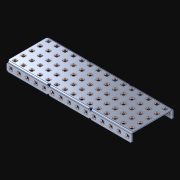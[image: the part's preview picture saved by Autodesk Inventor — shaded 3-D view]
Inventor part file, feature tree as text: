
AUTODESK INVENTOR PART (.ipt)
format: ipt  version: 2021 (Build 250183000, 183)  size: 1,814,016 bytes
history: native  units: in
note: dims shown in document units (in); Inventor stores cm internally (conversion verified against a paired STEP export)
features: extrude x106, other x106, sketch x4, pattern_linear x3
ambient origin geometry x8: Origin, YZ Plane, XZ Plane, XY Plane, X Axis, Y Axis, Z Axis, Center Point
bodies: Solid1 (feature_tree)
feature tree (219):
  pattern_linear  "Rectangular Pattern1"  Spacing1=0.182in  [1 undecoded]
  pattern_linear  "Rectangular Pattern2"  Spacing1=0.046in  [1 undecoded]
  pattern_linear  "Rectangular Pattern3"  Spacing1=0.5in  [1 undecoded]
  extrude  "Extrusion1"  Depth=0.046in
  sketch  "Sketch1"  dims[d0=0.182in]
  other  "Srf1"
  sketch  "Sketch2"  dims[d1=0.046in d2=0.0in]
  other  "Srf2"
  sketch  "Sketch3"  dims[d3=0.182in]
  other  "Srf3"
  other  "Srf4"
  other  "Srf5"
  other  "Srf6"
  other  "Srf7"
  other  "Srf8"
  other  "Srf9"
  other  "Srf10"
  other  "Srf11"
  other  "Srf12"
  other  "Srf13"
  other  "Srf14"
  other  "Srf15"
  other  "Srf16"
  other  "Srf17"
  other  "Srf38"
  other  "Srf39"
  other  "Srf40"
  other  "Srf41"
  other  "Srf42"
  other  "Srf43"
  other  "Srf44"
  other  "Srf45"
  other  "Srf46"
  other  "Srf47"
  other  "Srf48"
  other  "Srf49"
  other  "Srf50"
  other  "Srf51"
  other  "Srf72"
  other  "Srf73"
  other  "Srf74"
  other  "Srf75"
  other  "Srf76"
  other  "Srf77"
  other  "Srf78"
  other  "Srf79"
  other  "Srf80"
  other  "Srf81"
  other  "Srf82"
  other  "Srf83"
  other  "Srf84"
  other  "Srf85"
  other  "Srf86"
  other  "Srf107"
  other  "Srf108"
  other  "Srf109"
  other  "Srf110"
  other  "Srf111"
  other  "Srf112"
  other  "Srf113"
  other  "Srf114"
  other  "Srf115"
  other  "Srf116"
  other  "Srf117"
  other  "Srf118"
  other  "Srf119"
  other  "Srf120"
  other  "Srf121"
  other  "Srf142"
  other  "Srf143"
  other  "Srf144"
  other  "Srf145"
  other  "Srf146"
  other  "Srf147"
  other  "Srf148"
  other  "Srf149"
  other  "Srf150"
  other  "Srf151"
  other  "Srf152"
  other  "Srf153"
  other  "Srf154"
  other  "Srf155"
  other  "Srf156"
  other  "Srf177"
  other  "Srf178"
  other  "Srf179"
  other  "Srf180"
  other  "Srf181"
  other  "Srf182"
  other  "Srf183"
  other  "Srf184"
  other  "Srf185"
  other  "Srf186"
  other  "Srf187"
  other  "Srf188"
  other  "Srf189"
  other  "Srf190"
  other  "Srf191"
  other  "Srf212"
  other  "Srf213"
  other  "Srf214"
  other  "Srf215"
  other  "Srf216"
  other  "Srf217"
  other  "Srf218"
  other  "Srf219"
  other  "Srf220"
  other  "Srf221"
  other  "Srf222"
  other  "Srf223"
  other  "Srf224"
  other  "Srf225"
  sketch  "Sketch4"  dims[d4=0.046in d5=0.0in d6=0.182in d7=0.046in d8=0.0in d11=0.5in d12=5.9055in d14=0.5in d15=1.9685in d17=0.5in d18=5.9055in d20=0.5in d21=10.0in d22=0.0in]
  parser-record x1  (decoder bookkeeping rows leaked as tree rows — omitted from the tree; the rows remain in map.json)
  extrude  "ExtrusionSrf1"  Depth=0.046in
  extrude  "ExtrusionSrf2"  Depth=0.046in
  extrude  "ExtrusionSrf3"  Depth=0.046in
  extrude  "ExtrusionSrf4"  Depth=0.046in
  extrude  "ExtrusionSrf5"  Depth=0.046in
  extrude  "ExtrusionSrf6"  TaperAngle=0.0deg  [1 undecoded]
  extrude  "ExtrusionSrf7"  [1 undecoded]
  extrude  "ExtrusionSrf8"  [1 undecoded]
  extrude  "ExtrusionSrf9"  [1 undecoded]
  extrude  "ExtrusionSrf10"  [1 undecoded]
  extrude  "ExtrusionSrf11"  [1 undecoded]
  extrude  "ExtrusionSrf12"  [1 undecoded]
  extrude  "ExtrusionSrf13"  [1 undecoded]
  extrude  "ExtrusionSrf14"  [1 undecoded]
  extrude  "ExtrusionSrf15"  [1 undecoded]
  extrude  "ExtrusionSrf16"  [1 undecoded]
  extrude  "ExtrusionSrf17"  [1 undecoded]
  extrude  "ExtrusionSrf38"  [1 undecoded]
  extrude  "ExtrusionSrf39"  [1 undecoded]
  extrude  "ExtrusionSrf40"  [1 undecoded]
  extrude  "ExtrusionSrf41"  [1 undecoded]
  extrude  "ExtrusionSrf42"  [1 undecoded]
  extrude  "ExtrusionSrf43"  [1 undecoded]
  extrude  "ExtrusionSrf44"  [1 undecoded]
  extrude  "ExtrusionSrf45"  [1 undecoded]
  extrude  "ExtrusionSrf46"  [1 undecoded]
  extrude  "ExtrusionSrf47"  [1 undecoded]
  extrude  "ExtrusionSrf48"  [1 undecoded]
  extrude  "ExtrusionSrf49"  [1 undecoded]
  extrude  "ExtrusionSrf50"  [1 undecoded]
  extrude  "ExtrusionSrf51"  [1 undecoded]
  extrude  "ExtrusionSrf72"  [1 undecoded]
  extrude  "ExtrusionSrf73"  [1 undecoded]
  extrude  "ExtrusionSrf74"  [1 undecoded]
  extrude  "ExtrusionSrf75"  [1 undecoded]
  extrude  "ExtrusionSrf76"  [1 undecoded]
  extrude  "ExtrusionSrf77"  [1 undecoded]
  extrude  "ExtrusionSrf78"  [1 undecoded]
  extrude  "ExtrusionSrf79"  [1 undecoded]
  extrude  "ExtrusionSrf80"  [1 undecoded]
  extrude  "ExtrusionSrf81"  [1 undecoded]
  extrude  "ExtrusionSrf82"  [1 undecoded]
  extrude  "ExtrusionSrf83"  [1 undecoded]
  extrude  "ExtrusionSrf84"  [1 undecoded]
  extrude  "ExtrusionSrf85"  [1 undecoded]
  extrude  "ExtrusionSrf86"  [1 undecoded]
  extrude  "ExtrusionSrf107"  [1 undecoded]
  extrude  "ExtrusionSrf108"  [1 undecoded]
  extrude  "ExtrusionSrf109"  [1 undecoded]
  extrude  "ExtrusionSrf110"  [1 undecoded]
  extrude  "ExtrusionSrf111"  [1 undecoded]
  extrude  "ExtrusionSrf112"  [1 undecoded]
  extrude  "ExtrusionSrf113"  [1 undecoded]
  extrude  "ExtrusionSrf114"  [1 undecoded]
  extrude  "ExtrusionSrf115"  [1 undecoded]
  extrude  "ExtrusionSrf116"  [1 undecoded]
  extrude  "ExtrusionSrf117"  [1 undecoded]
  extrude  "ExtrusionSrf118"  [1 undecoded]
  extrude  "ExtrusionSrf119"  [1 undecoded]
  extrude  "ExtrusionSrf120"  [1 undecoded]
  extrude  "ExtrusionSrf121"  [1 undecoded]
  extrude  "ExtrusionSrf142"  [1 undecoded]
  extrude  "ExtrusionSrf143"  [1 undecoded]
  extrude  "ExtrusionSrf144"  [1 undecoded]
  extrude  "ExtrusionSrf145"  [1 undecoded]
  extrude  "ExtrusionSrf146"  [1 undecoded]
  extrude  "ExtrusionSrf147"  [1 undecoded]
  extrude  "ExtrusionSrf148"  [1 undecoded]
  extrude  "ExtrusionSrf149"  [1 undecoded]
  extrude  "ExtrusionSrf150"  [1 undecoded]
  extrude  "ExtrusionSrf151"  [1 undecoded]
  extrude  "ExtrusionSrf152"  [1 undecoded]
  extrude  "ExtrusionSrf153"  [1 undecoded]
  extrude  "ExtrusionSrf154"  [1 undecoded]
  extrude  "ExtrusionSrf155"  [1 undecoded]
  extrude  "ExtrusionSrf156"  [1 undecoded]
  extrude  "ExtrusionSrf177"  [1 undecoded]
  extrude  "ExtrusionSrf178"  [1 undecoded]
  extrude  "ExtrusionSrf179"  [1 undecoded]
  extrude  "ExtrusionSrf180"  [1 undecoded]
  extrude  "ExtrusionSrf181"  [1 undecoded]
  extrude  "ExtrusionSrf182"  [1 undecoded]
  extrude  "ExtrusionSrf183"  [1 undecoded]
  extrude  "ExtrusionSrf184"  [1 undecoded]
  extrude  "ExtrusionSrf185"  [1 undecoded]
  extrude  "ExtrusionSrf186"  [1 undecoded]
  extrude  "ExtrusionSrf187"  [1 undecoded]
  extrude  "ExtrusionSrf188"  [1 undecoded]
  extrude  "ExtrusionSrf189"  [1 undecoded]
  extrude  "ExtrusionSrf190"  [1 undecoded]
  extrude  "ExtrusionSrf191"  [1 undecoded]
  extrude  "ExtrusionSrf212"  [1 undecoded]
  extrude  "ExtrusionSrf213"  [1 undecoded]
  extrude  "ExtrusionSrf214"  [1 undecoded]
  extrude  "ExtrusionSrf215"  [1 undecoded]
  extrude  "ExtrusionSrf216"  [1 undecoded]
  extrude  "ExtrusionSrf217"  [1 undecoded]
  extrude  "ExtrusionSrf218"  [1 undecoded]
  extrude  "ExtrusionSrf219"  [1 undecoded]
  extrude  "ExtrusionSrf220"  [1 undecoded]
  extrude  "ExtrusionSrf221"  [1 undecoded]
  extrude  "ExtrusionSrf222"  [1 undecoded]
  extrude  "ExtrusionSrf223"  [1 undecoded]
  extrude  "ExtrusionSrf224"  [1 undecoded]
  extrude  "ExtrusionSrf225"  [1 undecoded]
note: 103 required parameter values undecoded (feature->parameter linkage not recoverable at this tier; creation-order binding heuristic only, values carry confidence <= 0.55)
